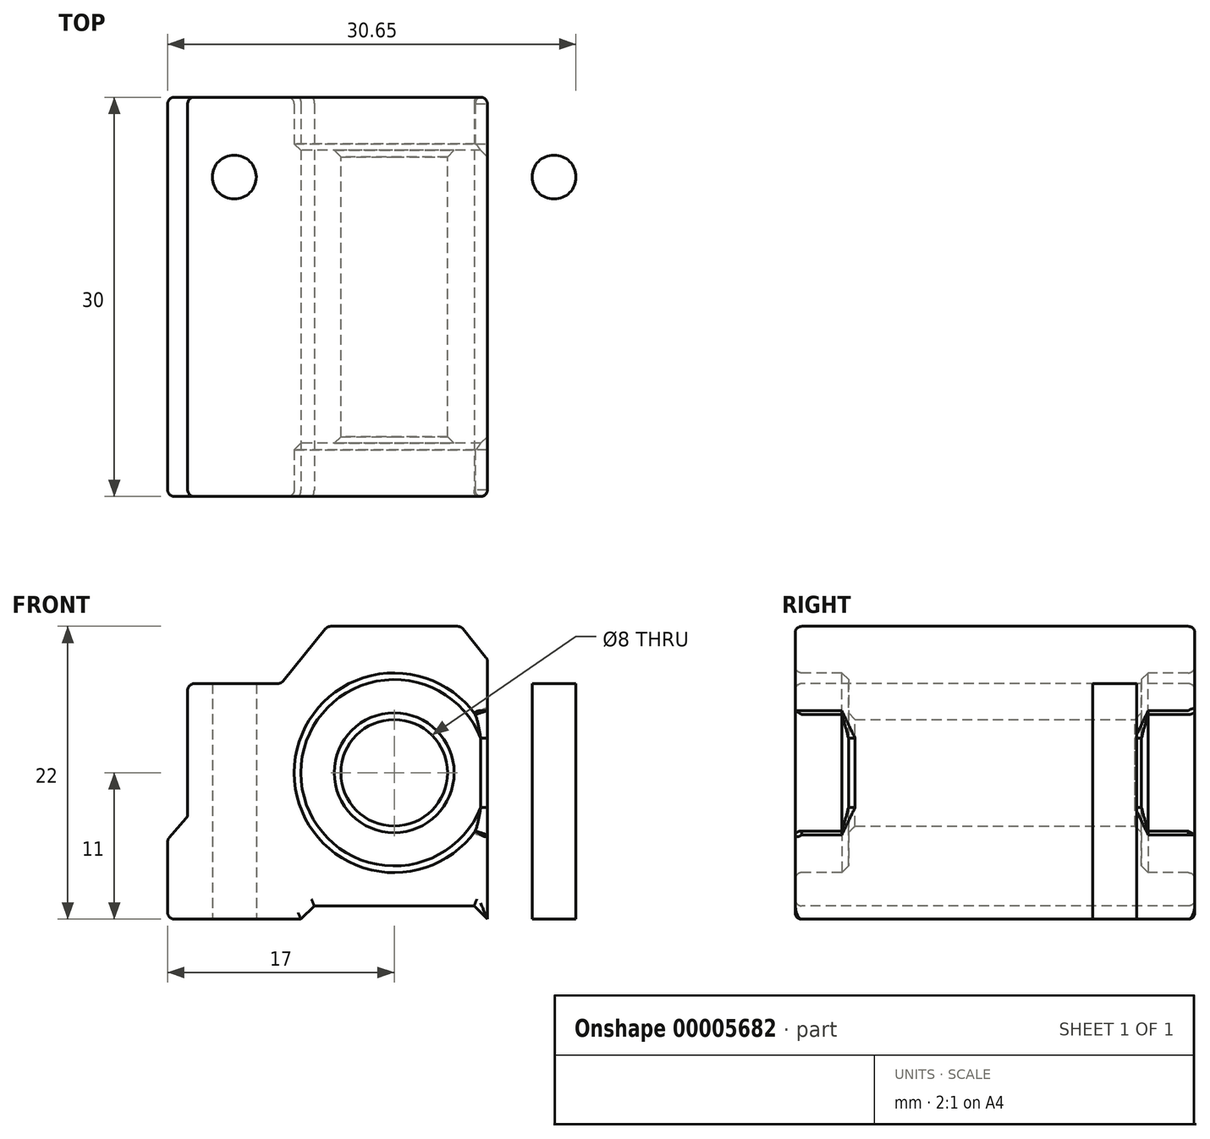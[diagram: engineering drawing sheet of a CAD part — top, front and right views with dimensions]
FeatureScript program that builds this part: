
annotation { "Feature Type Name" : "Feature", "Feature Type Description" : "" }
export const myFeature = defineFeature(function(context is Context, id is Id, definition is map)
    precondition{}
    {
        {
            var Q0;
            Q0=qCreatedBy(makeId("Front.planeOp"),FACE);
            var sketch = newSketch(context, id + "F0", { "sketchPlane" : qUnion([Q0])});
            skLineSegment(sketch, "E0.rect.bottom", {"start": v(17, 0) * mm, "end": v(7, 0) * mm});
            skLineSegment(sketch, "E0.rect.top", {"start": v(5, 22) * mm, "end": v(-5, 22) * mm});
            skLineSegment(sketch, "E0.rect.left", {"start": v(17, 0) * mm, "end": v(17, 6) * mm});
            skLineSegment(sketch, "E0.rect.right", {"start": v(-17, 0) * mm, "end": v(-17, 6) * mm});
            skPoint(sketch, "E0.rect.middle", {"position": v(0, 11) * mm});
            skCircle(sketch, "E1", {"center": v(0, 11) * mm, "radius": 4 * mm});
            skLineSegment(sketch, "E2", {"start": v(0, 22) * mm, "end": v(0, 0) * mm, "construction": true});
            skLineSegment(sketch, "E3", {"start": v(0, 22) * mm, "end": v(5, 22) * mm});
            skLineSegment(sketch, "E4", {"start": v(5, 22) * mm, "end": v(8.5, 17.7) * mm});
            skLineSegment(sketch, "E5", {"start": v(8.5, 17.7) * mm, "end": v(15.5, 17.7) * mm});
            skCircle(sketch, "E6", {"center": v(0, 11) * mm, "radius": 7.5 * mm});
            skLineSegment(sketch, "E7.0.MirrorCS", {"start": v(-5, 22) * mm, "end": v(-8.5, 17.7) * mm});
            skLineSegment(sketch, "E8.0.MirrorCS", {"start": v(-8.5, 17.7) * mm, "end": v(-15.5, 17.7) * mm});
            skLineSegment(sketch, "E9", {"start": v(0, 1) * mm, "end": v(6, 1) * mm});
            skLineSegment(sketch, "E10", {"start": v(6, 1) * mm, "end": v(7, 0) * mm});
            skLineSegment(sketch, "E11.0.MirrorCS", {"start": v(0, 1) * mm, "end": v(-6, 1) * mm});
            skLineSegment(sketch, "E12.0.MirrorCS", {"start": v(-6, 1) * mm, "end": v(-7, 0) * mm});
            skLineSegment(sketch, "E13.trimOffspring", {"start": v(-7, 0) * mm, "end": v(-17, 0) * mm});
            skLineSegment(sketch, "E14", {"start": v(15.5, 17.7) * mm, "end": v(15.5, 7.7) * mm});
            skLineSegment(sketch, "E15", {"start": v(15.5, 7.7) * mm, "end": v(17, 6) * mm});
            skLineSegment(sketch, "E16.0.MirrorCS", {"start": v(-15.5, 17.7) * mm, "end": v(-15.5, 7.7) * mm});
            skLineSegment(sketch, "E17.0.MirrorCS", {"start": v(-15.5, 7.7) * mm, "end": v(-17, 6) * mm});
            skSolve(sketch);
        }
        {
            var Q0;
            Q0=makeQuery(id+"F0.imprint","IMPRINT",FACE,{"disambiguationData":[TD([[makeQuery(id+"F0.imprint","IMPRINT",EDGE,{"derivedFrom":sQuery(id+"F0.wireOp",EDGE,"E0.rect.bottom")}),-1.0]])]});
            extrude(context, id + "F1", {"entities" : qUnion([Q0]), "oppositeDirection" : true, "depth" : 30 * mm, "symmetric" : true});
        }
        {
            var Q0;
            Q0=makeQuery(id+"F0.imprint","IMPRINT",FACE,{"disambiguationData":[TD([[makeQuery(id+"F0.imprint","IMPRINT",EDGE,{"derivedFrom":sQuery(id+"F0.wireOp",EDGE,"E1")}),-1.0]])]});
            extrude(context, id + "F2", {"entities" : qUnion([Q0]), "operationType" : NewBodyOperationType.ADD, "depth" : 22 * mm, "symmetric" : true});
        }
        {
            var Q0;
            Q0=makeQuery(id+"F1.opExtrude","SWEPT_FACE",FACE,{"disambiguationData":[OSD([sQuery(id+"F0.wireOp",EDGE,"E0.rect.bottom")])]});
            var sketch = newSketch(context, id + "F3", { "sketchPlane" : qUnion([Q0])});
            skCircle(sketch, "E18", {"center": v(12, 9) * mm, "radius": 1.65 * mm});
            skLineSegment(sketch, "E19", {"start": v(0, 15) * mm, "end": v(0, -15) * mm, "construction": true});
            skCircle(sketch, "E20.0.MirrorC", {"center": v(-12, 9) * mm, "radius": 1.65 * mm});
            skLineSegment(sketch, "E21", {"start": v(-17, 0) * mm, "end": v(17, 0) * mm, "construction": true});
            skCircle(sketch, "E22.0.MirrorC", {"center": v(12, -9) * mm, "radius": 1.65 * mm});
            skCircle(sketch, "E23.0.MirrorC", {"center": v(-12, -9) * mm, "radius": 1.65 * mm});
            skSolve(sketch);
        }
        {
            var Q0;
            Q0=makeQuery(id+"F3.imprint","IMPRINT",FACE,{"disambiguationData":[TD([[makeQuery(id+"F3.imprint","IMPRINT",EDGE,{"derivedFrom":sQuery(id+"F3.wireOp",EDGE,"E20.0.MirrorC")}),-1.0]])]});
            var Q1;
            Q1=makeQuery(id+"F3.imprint","IMPRINT",FACE,{"disambiguationData":[TD([[makeQuery(id+"F3.imprint","IMPRINT",EDGE,{"derivedFrom":sQuery(id+"F3.wireOp",EDGE,"E18")}),1.0]])]});
            var Q2;
            Q2=makeQuery(id+"F3.imprint","IMPRINT",FACE,{"disambiguationData":[TD([[makeQuery(id+"F3.imprint","IMPRINT",EDGE,{"derivedFrom":sQuery(id+"F3.wireOp",EDGE,"E23.0.MirrorC")}),1.0]])]});
            var Q3;
            Q3=makeQuery(id+"F3.imprint","IMPRINT",FACE,{"disambiguationData":[TD([[makeQuery(id+"F3.imprint","IMPRINT",EDGE,{"derivedFrom":sQuery(id+"F3.wireOp",EDGE,"E22.0.MirrorC")}),-1.0]])]});
            extrude(context, id + "F4", {"entities" : qUnion([Q0, Q1, Q2, Q3]), "operationType" : NewBodyOperationType.REMOVE, "oppositeDirection" : true, "depth" : 25 * mm});
        }
        {
            var Q0;
            Q0=makeQuery(id+"F1.opExtrude","CAP_FACE",FACE,{"disambiguationData":[OSD([sQuery(id+"F0.wireOp",EDGE,"E0.rect.bottom"),sQuery(id+"F0.wireOp",EDGE,"E0.rect.top"),sQuery(id+"F0.wireOp",EDGE,"E0.rect.left"),sQuery(id+"F0.wireOp",EDGE,"E0.rect.right"),sQuery(id+"F0.wireOp",EDGE,"E3"),sQuery(id+"F0.wireOp",EDGE,"E4"),sQuery(id+"F0.wireOp",EDGE,"E5"),sQuery(id+"F0.wireOp",EDGE,"E6"),sQuery(id+"F0.wireOp",EDGE,"E7.0.MirrorCS"),sQuery(id+"F0.wireOp",EDGE,"E8.0.MirrorCS"),sQuery(id+"F0.wireOp",EDGE,"E9"),sQuery(id+"F0.wireOp",EDGE,"E10"),sQuery(id+"F0.wireOp",EDGE,"E11.0.MirrorCS"),sQuery(id+"F0.wireOp",EDGE,"E12.0.MirrorCS"),sQuery(id+"F0.wireOp",EDGE,"E13.trimOffspring"),sQuery(id+"F0.wireOp",EDGE,"E14"),sQuery(id+"F0.wireOp",EDGE,"E15"),sQuery(id+"F0.wireOp",EDGE,"E16.0.MirrorCS"),sQuery(id+"F0.wireOp",EDGE,"E17.0.MirrorCS")])],"isStart":true});
            var Q1;
            Q1=makeQuery(id+"F1.opExtrude","CAP_FACE",FACE,{"disambiguationData":[OSD([sQuery(id+"F0.wireOp",EDGE,"E0.rect.bottom"),sQuery(id+"F0.wireOp",EDGE,"E0.rect.top"),sQuery(id+"F0.wireOp",EDGE,"E0.rect.left"),sQuery(id+"F0.wireOp",EDGE,"E0.rect.right"),sQuery(id+"F0.wireOp",EDGE,"E3"),sQuery(id+"F0.wireOp",EDGE,"E4"),sQuery(id+"F0.wireOp",EDGE,"E5"),sQuery(id+"F0.wireOp",EDGE,"E6"),sQuery(id+"F0.wireOp",EDGE,"E7.0.MirrorCS"),sQuery(id+"F0.wireOp",EDGE,"E8.0.MirrorCS"),sQuery(id+"F0.wireOp",EDGE,"E9"),sQuery(id+"F0.wireOp",EDGE,"E10"),sQuery(id+"F0.wireOp",EDGE,"E11.0.MirrorCS"),sQuery(id+"F0.wireOp",EDGE,"E12.0.MirrorCS"),sQuery(id+"F0.wireOp",EDGE,"E13.trimOffspring"),sQuery(id+"F0.wireOp",EDGE,"E14"),sQuery(id+"F0.wireOp",EDGE,"E15"),sQuery(id+"F0.wireOp",EDGE,"E16.0.MirrorCS"),sQuery(id+"F0.wireOp",EDGE,"E17.0.MirrorCS")])],"isStart":false});
            var Q2;
            Q2=makeQuery(id+"F1.opExtrude","SWEPT_FACE",FACE,{"disambiguationData":[OSD([sQuery(id+"F0.wireOp",EDGE,"E14")])]});
            var Q3;
            Q3=makeQuery(id+"F1.opExtrude","SWEPT_FACE",FACE,{"disambiguationData":[OSD([sQuery(id+"F0.wireOp",EDGE,"E0.rect.left")])]});
            var Q4;
            Q4=makeQuery(id+"F1.opExtrude","SWEPT_FACE",FACE,{"disambiguationData":[OSD([sQuery(id+"F0.wireOp",EDGE,"E4")])]});
            var Q5;
            Q5=makeQuery(id+"F1.opExtrude","SWEPT_FACE",FACE,{"disambiguationData":[OSD([sQuery(id+"F0.wireOp",EDGE,"E0.rect.right")])]});
            var Q6;
            Q6=makeQuery(id+"F1.opExtrude","SWEPT_FACE",FACE,{"disambiguationData":[OSD([sQuery(id+"F0.wireOp",EDGE,"E16.0.MirrorCS")])]});
            var Q7;
            Q7=makeQuery(id+"F1.opExtrude","SWEPT_FACE",FACE,{"disambiguationData":[OSD([sQuery(id+"F0.wireOp",EDGE,"E7.0.MirrorCS")])]});
            fillet(context, id + "F5", {"entities" : qUnion([Q0, Q1, Q2, Q3, Q4, Q5, Q6, Q7]), "radius" : .5 * mm, "tangentPropagation" : true, "allowEdgeOverflow" : false});
        }
        {
            var Q0;
            Q0=makeQuery(id+"F2.opExtrude","CAP_FACE",FACE,{"disambiguationData":[OSD([sQuery(id+"F0.wireOp",EDGE,"E1"),sQuery(id+"F0.wireOp",EDGE,"E6")])],"isStart":false});
            var Q1;
            Q1=makeQuery(id+"F2.opExtrude","CAP_FACE",FACE,{"disambiguationData":[OSD([sQuery(id+"F0.wireOp",EDGE,"E1"),sQuery(id+"F0.wireOp",EDGE,"E6")])],"isStart":true});
            chamfer(context, id + "F6", {"entities" : qUnion([Q0, Q1]), "width" : .5 * mm, "tangentPropagation" : true});
        }
        {
            var Q0;
            Q0=makeQuery(id+"F1.opExtrude","SWEPT_FACE",FACE,{"disambiguationData":[OSD([sQuery(id+"F0.wireOp",EDGE,"E8.0.MirrorCS")])]});
            var Q1;
            {var subQ0=sQuery(id+"F0.wireOp",EDGE,"E7.0.MirrorCS");Q1=makeQuery(id+"F5.opFillet","BLEND_EDGE",EDGE,{"blendedFrom":[makeQuery(id+"F1.opExtrude","SWEPT_EDGE",EDGE,{"disambiguationData":[OSD([sQuery(id+"F0.wireOp",EDGE,"E0.rect.top"),subQ0])]}),makeQuery(id+"F1.opExtrude","SWEPT_FACE",FACE,{"disambiguationData":[OSD([subQ0])]})],"blendedInto":[makeQuery(id+"F1.opExtrude","SWEPT_FACE",FACE,{"disambiguationData":[OSD([subQ0])]})]});}
            revolve(context, id + "F7", {"entities" : qUnion([Q0]), "axis" : qUnion([Q1]), "revolveType" : RevolveType.ONE_DIRECTION, "oppositeDirection" : true, "angle" : 51.02 * degree});
        }
        {
            var Q0;
            Q0=makeQuery(id+"F7.opRevolve","SWEPT_BODY",BODY,{"disambiguationData":[OSD([sQuery(id+"F0.wireOp",EDGE,"E8.0.MirrorCS")])]});
            deleteBodies(context, id + "F8", {"entities" : qUnion([Q0])});
        }
    });
